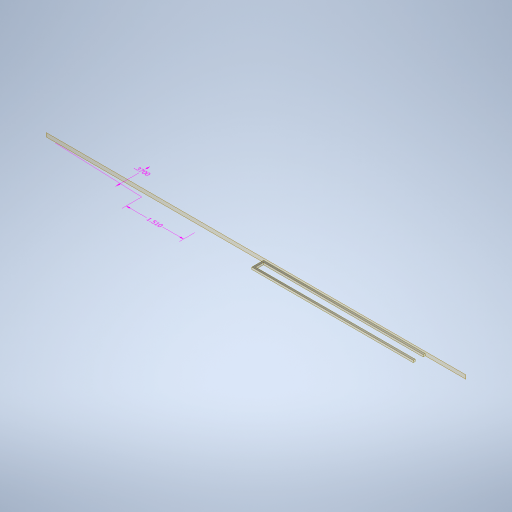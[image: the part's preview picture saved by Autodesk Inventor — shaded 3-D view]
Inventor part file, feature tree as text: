
AUTODESK INVENTOR PART (.ipt)
format: ipt  version: 2024.2 (Build 282272000, 272)  size: 275,456 bytes
history: native  units: in
note: dims shown in document units (in); Inventor stores cm internally (conversion verified against a paired STEP export)
features: other x3, plane x3, sketch x2, sweep x1
ambient origin geometry x8: Origin, YZ Plane, XZ Plane, XY Plane, X Axis, Y Axis, Z Axis, Center Point
bodies: Solid1 (feature_tree)
feature tree (9):
  other  "Annotations"
  sweep  "Sweep1"
  plane  "Work Plane1"
  plane  "Work Plane2"
  plane  "Work Plane4"
  sketch  "Sketch1"  dims[d6=0.0in d7=0.0in d11=0.25in d19=-0.25in]
  sketch  "Sketch2"  dims[d69=1.625in d70=1.625in d86=-0.1175in d89=0.1in d90=0.0in d91=0.0in d92=0.0in d98=0.02in d99=0.02in d42=0.2341in d43=0.169in d44=0.37in d48=0.2141in d49=0.2512in d50=1.51in]
  other  "Linear Dimension 1"
  other  "Linear Dimension 3"
